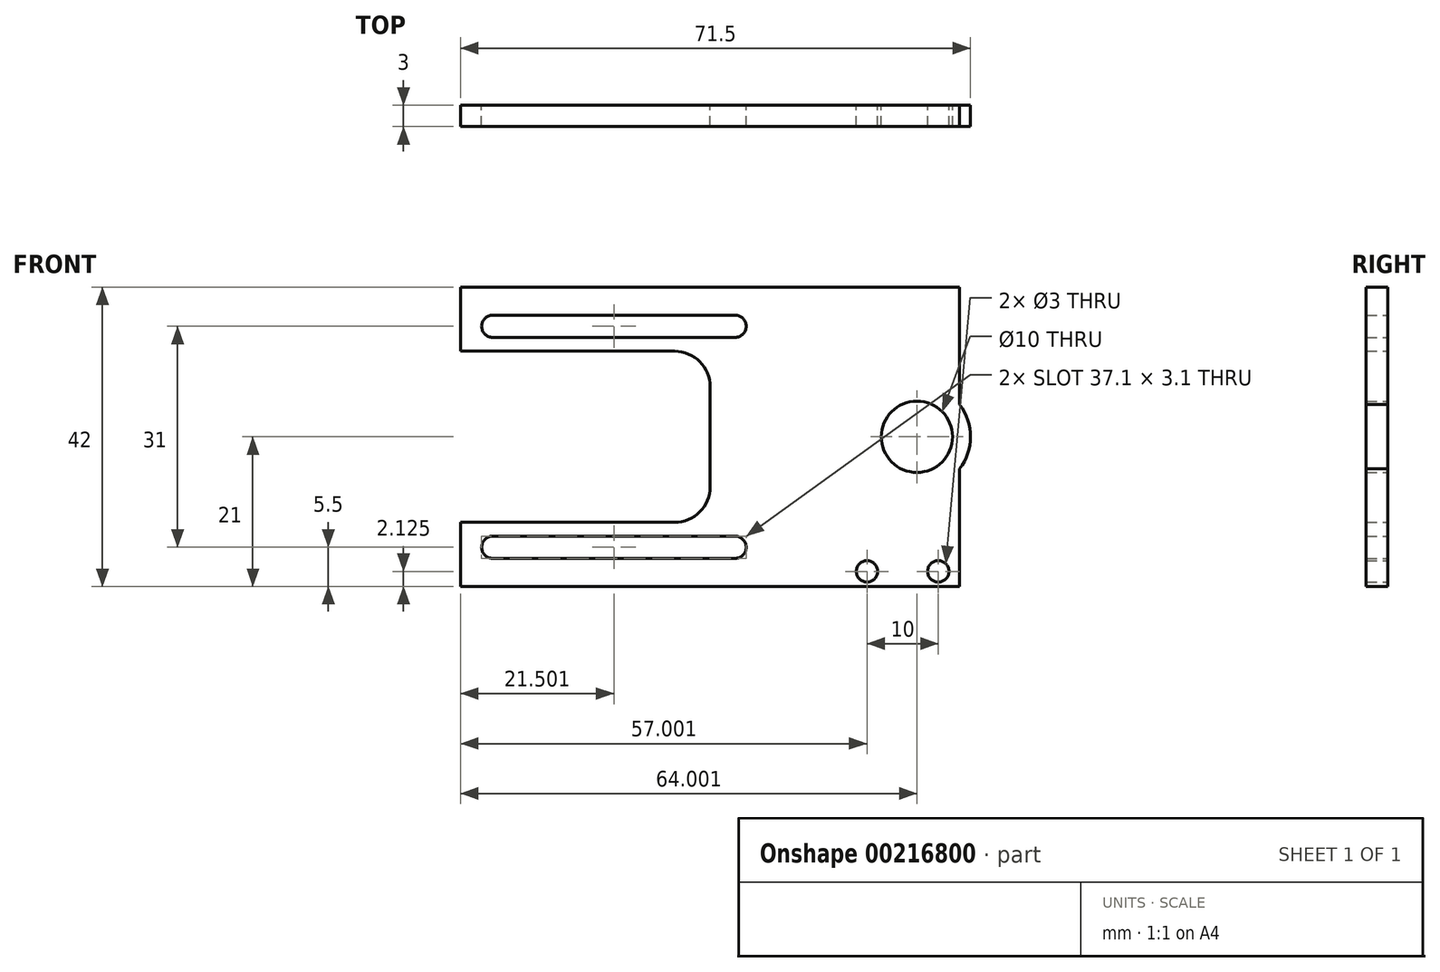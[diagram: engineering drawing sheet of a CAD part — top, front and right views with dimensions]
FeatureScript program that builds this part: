
annotation { "Feature Type Name" : "Feature", "Feature Type Description" : "" }
export const myFeature = defineFeature(function(context is Context, id is Id, definition is map)
    precondition{}
    {
        {
            var Q0;
            Q0=qCreatedBy(makeId("Front.planeOp"),FACE);
            var sketch = newSketch(context, id + "F0", { "sketchPlane" : qUnion([Q0])});
            skLineSegment(sketch, "E0.bottom", {"start": v(-40.8, 21) * mm, "end": v(29.2, 21) * mm});
            skLineSegment(sketch, "E0.top", {"start": v(-40.8, -21) * mm, "end": v(29.2, -21) * mm});
            skLineSegment(sketch, "E0.left", {"start": v(-40.8, 21) * mm, "end": v(-40.8, -21) * mm});
            skLineSegment(sketch, "E0.right", {"start": v(29.2, 21) * mm, "end": v(29.2, -21) * mm});
            skPoint(sketch, "E1", {"position": v(29.2, 0) * mm});
            skLineSegment(sketch, "E2.bottom", {"start": v(-40.8, 12) * mm, "end": v(-10.8, 12) * mm});
            skLineSegment(sketch, "E2.top", {"start": v(-40.8, -12) * mm, "end": v(-10.8, -12) * mm});
            skLineSegment(sketch, "E2.left", {"start": v(-40.8, 12) * mm, "end": v(-40.8, -12) * mm});
            skLineSegment(sketch, "E2.right", {"start": v(-5.8, 7) * mm, "end": v(-5.8, -7) * mm});
            skPoint(sketch, "E3", {"position": v(-5.8, 0) * mm});
            skPoint(sketch, "E4.visualSharp", {"position": v(-5.8, 12) * mm});
            skArc(sketch, "E4.filletArc", {"start": v(-5.8, 7) * mm, "mid": v(-7.26, 10.54) * mm, "end": v(-10.8, 12) * mm});
            skPoint(sketch, "E5.visualSharp", {"position": v(-5.8, -12) * mm});
            skArc(sketch, "E5.filletArc", {"start": v(-10.8, -12) * mm, "mid": v(-7.26, -10.54) * mm, "end": v(-5.8, -7) * mm});
            skLineSegment(sketch, "E6.bottom", {"start": v(-36.3, 17.05) * mm, "end": v(-2.3, 17.05) * mm});
            skLineSegment(sketch, "E6.top", {"start": v(-36.3, 13.95) * mm, "end": v(-2.3, 13.95) * mm});
            skLineSegment(sketch, "E6.left", {"start": v(-36.3, 17.05) * mm, "end": v(-36.3, 13.95) * mm});
            skLineSegment(sketch, "E6.right", {"start": v(-2.3, 17.05) * mm, "end": v(-2.3, 13.95) * mm});
            skPoint(sketch, "E7", {"position": v(-36.3, 15.5) * mm});
            skCircle(sketch, "E8", {"center": v(-36.3, 15.5) * mm, "radius": 1.55 * mm});
            skPoint(sketch, "E9", {"position": v(-2.3, 15.5) * mm});
            skCircle(sketch, "E10", {"center": v(-2.3, 15.5) * mm, "radius": 1.55 * mm});
            skLineSegment(sketch, "E11", {"start": v(-40.8, 0) * mm, "end": v(-5.8, 0) * mm, "construction": true});
            skLineSegment(sketch, "E12.MirrorCS", {"start": v(-36.3, -17.05) * mm, "end": v(-36.3, -13.95) * mm});
            skLineSegment(sketch, "E13.MirrorCS", {"start": v(-2.3, -17.05) * mm, "end": v(-2.3, -13.95) * mm});
            skLineSegment(sketch, "E14.MirrorCS", {"start": v(-36.3, -13.95) * mm, "end": v(-2.3, -13.95) * mm});
            skLineSegment(sketch, "E15.MirrorCS", {"start": v(-36.3, -17.05) * mm, "end": v(-2.3, -17.05) * mm});
            skCircle(sketch, "E16.MirrorC", {"center": v(-2.3, -15.5) * mm, "radius": 1.55 * mm});
            skCircle(sketch, "E17.MirrorC", {"center": v(-36.3, -15.5) * mm, "radius": 1.55 * mm});
            skPoint(sketch, "E18", {"position": v(23.2, 0) * mm});
            skPoint(sketch, "E19", {"position": v(26.2, -18.87) * mm});
            skPoint(sketch, "E20", {"position": v(16.2, -18.87) * mm});
            skCircle(sketch, "E21", {"center": v(23.2, 0) * mm, "radius": 5 * mm});
            skCircle(sketch, "E22", {"center": v(23.2, 0) * mm, "radius": 7.5 * mm});
            skSolve(sketch);
        }
        {
            var Q0;
            {var subQ2=sQuery(id+"F0.wireOp",EDGE,"E0.bottom");Q0=makeQuery(id+"F0.imprint","IMPRINT",FACE,{"disambiguationData":[TD([[makeQuery(id+"F0.imprint","IMPRINT",EDGE,{"derivedFrom":subQ2}),-1.0]])]});}
            var Q1;
            {var subQ0=sQuery(id+"F0.wireOp",EDGE,"E22");var subQ1=sQuery(id+"F0.wireOp",EDGE,"E0.right");var subQ2=makeQuery(id+"F0.imprint","INTERSECT",VERTEX,{"disambiguationData":[OD(0.0)],"derivedFrom":[subQ1,subQ0]});Q1=makeQuery(id+"F0.imprint","IMPRINT",FACE,{"disambiguationData":[TD([[makeQuery(id+"F0.imprint","IMPRINT",EDGE,{"disambiguationData":[TD([[subQ2,-1.0]])],"derivedFrom":subQ1}),1.0]])]});}
            var Q2;
            Q2=makeQuery(id+"F0.imprint","IMPRINT",FACE,{"disambiguationData":[TD([[makeQuery(id+"F0.imprint","IMPRINT",EDGE,{"derivedFrom":sQuery(id+"F0.wireOp",EDGE,"E21")}),-1.0]])]});
            extrude(context, id + "F1", {"entities" : qUnion([Q0, Q1, Q2]), "depth" : 3 * mm});
        }
        {
            var Q0;
            Q0=sQuery(id+"F0.wireOp",VERTEX,"E20");
            var Q1;
            Q1=sQuery(id+"F0.wireOp",VERTEX,"E19");
            var Q2;
            Q2=makeQuery(id+"F1.opExtrude","SWEPT_BODY",BODY,{"disambiguationData":[OSD([sQuery(id+"F0.wireOp",EDGE,"E0.bottom"),sQuery(id+"F0.wireOp",EDGE,"E0.top"),sQuery(id+"F0.wireOp",EDGE,"E0.left"),sQuery(id+"F0.wireOp",EDGE,"E0.right"),sQuery(id+"F0.wireOp",EDGE,"E2.bottom"),sQuery(id+"F0.wireOp",EDGE,"E2.top"),sQuery(id+"F0.wireOp",EDGE,"E2.right"),sQuery(id+"F0.wireOp",EDGE,"E4.filletArc"),sQuery(id+"F0.wireOp",EDGE,"E5.filletArc"),sQuery(id+"F0.wireOp",EDGE,"E6.bottom"),sQuery(id+"F0.wireOp",EDGE,"E6.top"),sQuery(id+"F0.wireOp",EDGE,"E8"),sQuery(id+"F0.wireOp",EDGE,"E10"),sQuery(id+"F0.wireOp",EDGE,"E14.MirrorCS"),sQuery(id+"F0.wireOp",EDGE,"E15.MirrorCS"),sQuery(id+"F0.wireOp",EDGE,"E16.MirrorC"),sQuery(id+"F0.wireOp",EDGE,"E17.MirrorC")])]});
            hole(context, id + "F2", {"style" : HoleStyle.SIMPLE, "endStyle" : HoleEndStyle.THROUGH, "oppositeDirection" : true, "holeDiameter" : 3 * mm, "locations" : qUnion([Q0, Q1]), "scope" : qUnion([Q2]), "isTappedThrough" : true});
        }
    });
